# Revit family: FW-IP30-Without_Door-With_notch-leer-AT-de
name_source: partatom
category: Electrical Equipment
units: mm (PartAtom-declared; Revit-internal decimal feet)

## family parameters
Cut with Voids When Loaded = No
Host = Face
Panel Configuration = Two Columns, Circuits Across
Part Type = Panelboard
Room Calculation Point = No
Round Connector Dimension = Use Diameter
Shared = No

## types (16) — shared parameters
EF000003 - Montageart = EV000128 - Hohlwand
EF000007 - Farbe = EV000202 - weiß
EF000049 - Tiefe = 125 mm  [stored 0.410105 ft]
EF000116 - RAL-Nummer = 0
EF000118 - Mit Montageplatte = No
EF000218 - Einbautiefe = 112 mm  [stored 0.367454 ft]
EF000339 - Art der Abdeckung = EV000494 - ohne
EF001062 - EMV-Ausführung = No
EF001088 - Anbaumöglichkeit = No
EF001131 - Innentiefe = 112 mm  [stored 0.367454 ft]
EF001134 - DIN-Schiene = No
EF001596 - Werkstoff des Gehäuses = 0
EF004462 - Art der Schließung = EV000154 - sonstige
EF005474 - Schutzart (IP) = EV006410 - IP30
EF006244 - Transparenter Deckel/Tür = Yes
EF006306 - Mit Schloss = No
EF009212 - Ausführung Deckel = EV009916 - mit Ausschnitt
EF015776 - Erdungsklemmenblock = No
EF015777 - Neutralleiterklemmenblock = No
EF015941 - Signaldurchlassende Tür = No
HG000002 - Mit tür = No
HG000003 - Bereich = FW
HG000005 - Dicke = 3 mm  [stored 0.00984252 ft]
HG000006 - Unterputz = Yes
HG000009 - Doppelflügeligen Tür = No
HG000010 - Asymmetrische Türen = No
HG000011 - Leere Reihen von unten = No
Manufacturer = Hager
Type Comments = FW
zero-valued in all types: Default Elevation, EF000266 - Anzahl der Reihen, EF002950 - Breite in Teilungseinheiten, HG000001 - Anzahl der Spalten, HG000007 - Anzahl der leeren Spalten, HG000008 - Anzahl der leeren Reihen

## per-type parameters (varying)
| type | EF000008 - Breite | EF000040 - Höhe | EF000332 - Einbauhöhe | EF000846 - Einbaubreite | HG000004 - Herstellerreferenz | Model |
| Unterputz IP30 B353 H1003 T125 0 Teilungseinheiten - FWU61L | 353 mm  [stored 1.15814 ft] | 1003 mm  [stored 3.29068 ft] | 952 mm  [stored 3.12336 ft] | 310 mm  [stored 1.01706 ft] | FWU61L | FWU61L |
| Unterputz IP30 B353 H1153 T125 0 Teilungseinheiten - FWU71L | 353 mm  [stored 1.15814 ft] | 1153 mm | 1102 mm  [stored 3.61549 ft] | 310 mm  [stored 1.01706 ft] | FWU71L | FWU71L |
| Unterputz IP30 B353 H1303 T125 0 Teilungseinheiten - FWU81L | 353 mm  [stored 1.15814 ft] | 1303 mm  [stored 4.27493 ft] | 1252 mm  [stored 4.10761 ft] | 310 mm  [stored 1.01706 ft] | FWU81L | FWU81L |
| Unterputz IP30 B353 H553 T125 0 Teilungseinheiten - FWU31L | 353 mm  [stored 1.15814 ft] | 553 mm  [stored 1.8143 ft] | 502 mm  [stored 1.64698 ft] | 310 mm  [stored 1.01706 ft] | FWU31L | FWU31L |
| Unterputz IP30 B353 H703 T125 0 Teilungseinheiten - FWU41L | 353 mm  [stored 1.15814 ft] | 703 mm  [stored 2.30643 ft] | 652 mm  [stored 2.13911 ft] | 310 mm  [stored 1.01706 ft] | FWU41L | FWU41L |
| Unterputz IP30 B353 H853 T125 0 Teilungseinheiten - FWU51L | 353 mm  [stored 1.15814 ft] | 853 mm  [stored 2.79856 ft] | 802 mm  [stored 2.63123 ft] | 310 mm  [stored 1.01706 ft] | FWU51L | FWU51L |
| Unterputz IP30 B603 H1003 T125 0 Teilungseinheiten - FWU62L | 603 mm | 1003 mm  [stored 3.29068 ft] | 952 mm  [stored 3.12336 ft] | 560 mm  [stored 1.83727 ft] | FWU62L | FWU62L |
| Unterputz IP30 B603 H1153 T125 0 Teilungseinheiten - FWU72L | 603 mm | 1153 mm | 1102 mm  [stored 3.61549 ft] | 560 mm  [stored 1.83727 ft] | FWU72L | FWU72L |
| Unterputz IP30 B603 H553 T125 0 Teilungseinheiten - FWU32L | 603 mm | 553 mm  [stored 1.8143 ft] | 502 mm  [stored 1.64698 ft] | 560 mm  [stored 1.83727 ft] | FWU32L | FWU32L |
| Unterputz IP30 B603 H703 T125 0 Teilungseinheiten - FWU42L | 603 mm | 703 mm  [stored 2.30643 ft] | 652 mm  [stored 2.13911 ft] | 560 mm  [stored 1.83727 ft] | FWU42L | FWU42L |
| Unterputz IP30 B603 H853 T125 0 Teilungseinheiten - FWU52L | 603 mm | 853 mm  [stored 2.79856 ft] | 802 mm  [stored 2.63123 ft] | 560 mm  [stored 1.83727 ft] | FWU52L | FWU52L |
| Unterputz IP30 B853 H1003 T125 0 Teilungseinheiten - FWU63L | 853 mm  [stored 2.79856 ft] | 1003 mm  [stored 3.29068 ft] | 952 mm  [stored 3.12336 ft] | 810 mm | FWU63L | FWU63L |
| Unterputz IP30 B853 H1153 T125 0 Teilungseinheiten - FWU73L | 853 mm  [stored 2.79856 ft] | 1153 mm | 1102 mm  [stored 3.61549 ft] | 810 mm | FWU73L | FWU73L |
| Unterputz IP30 B853 H553 T125 0 Teilungseinheiten - FWU33L | 853 mm  [stored 2.79856 ft] | 553 mm  [stored 1.8143 ft] | 502 mm  [stored 1.64698 ft] | 810 mm | FWU33L | FWU33L |
| Unterputz IP30 B853 H703 T125 0 Teilungseinheiten - FWU43L | 853 mm  [stored 2.79856 ft] | 703 mm  [stored 2.30643 ft] | 652 mm  [stored 2.13911 ft] | 810 mm | FWU43L | FWU43L |
| Unterputz IP30 B853 H853 T125 0 Teilungseinheiten - FWU53L | 853 mm  [stored 2.79856 ft] | 853 mm  [stored 2.79856 ft] | 802 mm  [stored 2.63123 ft] | 810 mm | FWU53L | FWU53L |

note: [stored X ft] marks values corroborated as IEEE doubles in the binary element streams (Revit-internal decimal feet)

## geometry (parser evidence)
native form markers: Sweep x12
no freeform markers — native parametric forms only
